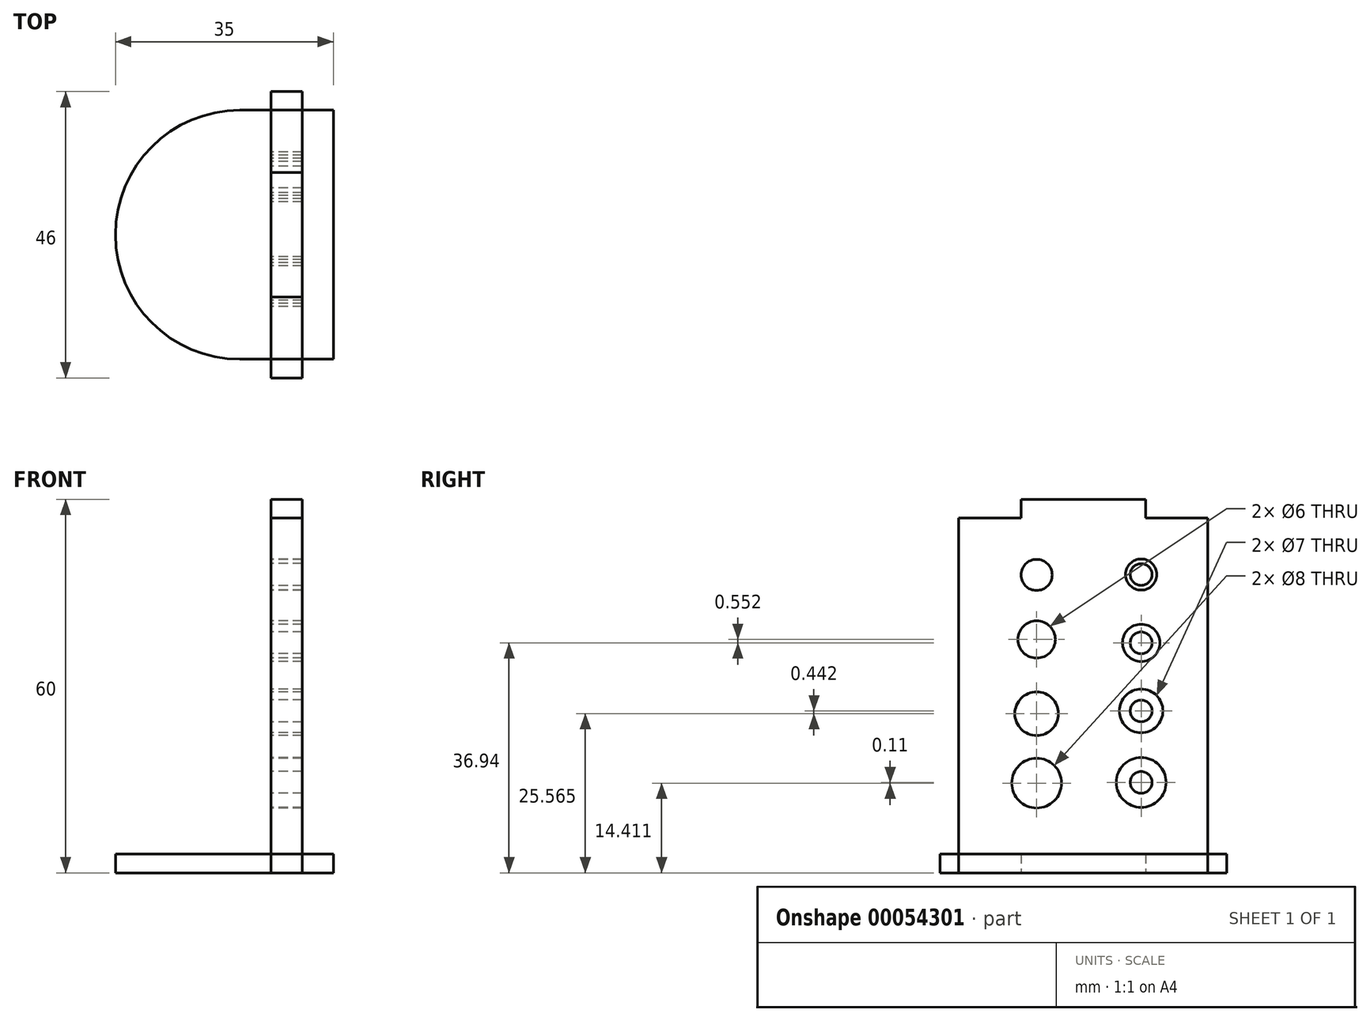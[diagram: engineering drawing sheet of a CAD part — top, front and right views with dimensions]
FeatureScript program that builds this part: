
annotation { "Feature Type Name" : "Feature", "Feature Type Description" : "" }
export const myFeature = defineFeature(function(context is Context, id is Id, definition is map)
    precondition{}
    {
        {
            var Q0;
            Q0=qCreatedBy(makeId("Top.planeOp"),FACE);
            var sketch = newSketch(context, id + "F0", { "sketchPlane" : qUnion([Q0])});
            skLineSegment(sketch, "E0.rect.bottom", {"start": v(7.5, 20) * mm, "end": v(-7.5, 20) * mm});
            skLineSegment(sketch, "E0.rect.top", {"start": v(7.5, -20) * mm, "end": v(-7.5, -20) * mm});
            skLineSegment(sketch, "E0.rect.left", {"start": v(7.5, 20) * mm, "end": v(7.5, -20) * mm});
            skLineSegment(sketch, "E0.rect.right", {"start": v(-7.5, 20) * mm, "end": v(-7.5, -20) * mm});
            skPoint(sketch, "E0.rect.middle", {"position": v(0, 0) * mm});
            skArc(sketch, "E1", {"start": v(-7.5, 20) * mm, "mid": v(-27.5, 0) * mm, "end": v(-7.5, -20) * mm});
            skLineSegment(sketch, "E2.bottom", {"start": v(-2.5, 20) * mm, "end": v(2.5, 20) * mm});
            skLineSegment(sketch, "E2.top", {"start": v(-2.5, 23) * mm, "end": v(2.5, 23) * mm});
            skLineSegment(sketch, "E2.left", {"start": v(-2.5, 20) * mm, "end": v(-2.5, 23) * mm});
            skLineSegment(sketch, "E2.right", {"start": v(2.5, 20) * mm, "end": v(2.5, 23) * mm});
            skLineSegment(sketch, "E3.bottom", {"start": v(-2.5, -20) * mm, "end": v(2.5, -20) * mm});
            skLineSegment(sketch, "E3.top", {"start": v(-2.5, -23) * mm, "end": v(2.5, -23) * mm});
            skLineSegment(sketch, "E3.left", {"start": v(-2.5, -20) * mm, "end": v(-2.5, -23) * mm});
            skLineSegment(sketch, "E3.right", {"start": v(2.5, -20) * mm, "end": v(2.5, -23) * mm});
            skLineSegment(sketch, "E4.bottom", {"start": v(2.5, 20) * mm, "end": v(7.5, 20) * mm});
            skLineSegment(sketch, "E4.top", {"start": v(2.5, 23) * mm, "end": v(7.5, 23) * mm});
            skLineSegment(sketch, "E4.right", {"start": v(7.5, 20) * mm, "end": v(7.5, 23) * mm});
            skLineSegment(sketch, "E5.bottom", {"start": v(2.5, -20) * mm, "end": v(7.5, -20) * mm});
            skLineSegment(sketch, "E5.top", {"start": v(2.5, -23) * mm, "end": v(7.5, -23) * mm});
            skLineSegment(sketch, "E5.right", {"start": v(7.5, -20) * mm, "end": v(7.5, -23) * mm});
            skLineSegment(sketch, "E6.bottom", {"start": v(-2.5, -23) * mm, "end": v(-7.5, -23) * mm});
            skLineSegment(sketch, "E6.top", {"start": v(-2.5, -20) * mm, "end": v(-7.5, -20) * mm});
            skLineSegment(sketch, "E6.left", {"start": v(-2.5, -23) * mm, "end": v(-2.5, -20) * mm});
            skLineSegment(sketch, "E6.right", {"start": v(-7.5, -23) * mm, "end": v(-7.5, -20) * mm});
            skLineSegment(sketch, "E7.bottom", {"start": v(-2.5, 23) * mm, "end": v(-7.5, 23) * mm});
            skLineSegment(sketch, "E7.top", {"start": v(-2.5, 20) * mm, "end": v(-7.5, 20) * mm});
            skLineSegment(sketch, "E7.left", {"start": v(-2.5, 23) * mm, "end": v(-2.5, 20) * mm});
            skLineSegment(sketch, "E7.right", {"start": v(-7.5, 23) * mm, "end": v(-7.5, 20) * mm});
            skArc(sketch, "E8", {"start": v(-7.5, 23) * mm, "mid": v(-30.5, 0) * mm, "end": v(-7.5, -23) * mm});
            skLineSegment(sketch, "E9", {"start": v(7.5, 21.5) * mm, "end": v(-7.5, 21.5) * mm, "construction": true});
            skLineSegment(sketch, "E10", {"start": v(7.5, -21.5) * mm, "end": v(-7.5, -21.5) * mm, "construction": true});
            skArc(sketch, "E11", {"start": v(-7.5, 21.5) * mm, "mid": v(-29, 0) * mm, "end": v(-7.5, -21.5) * mm, "construction": true});
            skLineSegment(sketch, "E12.rect.bottom", {"start": v(2.5, 10) * mm, "end": v(-2.5, 10) * mm});
            skLineSegment(sketch, "E12.rect.top", {"start": v(2.5, -10) * mm, "end": v(-2.5, -10) * mm});
            skLineSegment(sketch, "E12.rect.left", {"start": v(2.5, 10) * mm, "end": v(2.5, -10) * mm});
            skLineSegment(sketch, "E12.rect.right", {"start": v(-2.5, 10) * mm, "end": v(-2.5, -10) * mm});
            skLineSegment(sketch, "E13.rect.bottom", {"start": v(2.5, 20) * mm, "end": v(-2.5, 20) * mm});
            skLineSegment(sketch, "E13.rect.top", {"start": v(2.5, -20) * mm, "end": v(-2.5, -20) * mm});
            skLineSegment(sketch, "E13.rect.left", {"start": v(2.5, 20) * mm, "end": v(2.5, -20) * mm});
            skLineSegment(sketch, "E13.rect.right", {"start": v(-2.5, 20) * mm, "end": v(-2.5, -20) * mm});
            skSolve(sketch);
        }
        {
            var Q0;
            Q0=makeQuery(id+"F0.imprint","IMPRINT",FACE,{"disambiguationData":[TD([[makeQuery(id+"F0.imprint","IMPRINT",EDGE,{"derivedFrom":sQuery(id+"F0.wireOp",EDGE,"E0.rect.right")}),-1.0]])]});
            var Q1;
            Q1=makeQuery(id+"F0.imprint","IMPRINT",FACE,{"disambiguationData":[TD([[makeQuery(id+"F0.imprint","IMPRINT",EDGE,{"derivedFrom":sQuery(id+"F0.wireOp",EDGE,"E0.rect.left")}),-1.0]])]});
            var Q2;
            Q2=makeQuery(id+"F0.imprint","IMPRINT",FACE,{"disambiguationData":[TD([[makeQuery(id+"F0.imprint","IMPRINT",EDGE,{"derivedFrom":sQuery(id+"F0.wireOp",EDGE,"E2.bottom")}),1.0]])]});
            var Q3;
            Q3=makeQuery(id+"F0.imprint","IMPRINT",FACE,{"disambiguationData":[TD([[makeQuery(id+"F0.imprint","IMPRINT",EDGE,{"derivedFrom":sQuery(id+"F0.wireOp",EDGE,"E3.bottom")}),-1.0]])]});
            var Q4;
            Q4=makeQuery(id+"F0.imprint","IMPRINT",FACE,{"disambiguationData":[TD([[makeQuery(id+"F0.imprint","IMPRINT",EDGE,{"derivedFrom":sQuery(id+"F0.wireOp",EDGE,"E0.rect.right")}),1.0]])]});
            var Q5;
            {var subQ0=sQuery(id+"F0.wireOp",EDGE,"E12.rect.bottom");Q5=makeQuery(id+"F0.imprint","IMPRINT",FACE,{"disambiguationData":[TD([[makeQuery(id+"F0.imprint","IMPRINT",EDGE,{"derivedFrom":subQ0}),-1.0]])]});}
            var Q6;
            {var subQ0=sQuery(id+"F0.wireOp",EDGE,"E12.rect.top");Q6=makeQuery(id+"F0.imprint","IMPRINT",FACE,{"disambiguationData":[TD([[makeQuery(id+"F0.imprint","IMPRINT",EDGE,{"derivedFrom":subQ0}),1.0]])]});}
            var Q7;
            Q7=makeQuery(id+"F0.imprint","IMPRINT",FACE,{"disambiguationData":[TD([[makeQuery(id+"F0.imprint","IMPRINT",EDGE,{"derivedFrom":sQuery(id+"F0.wireOp",EDGE,"E2.top")}),-1.0]])]});
            var Q8;
            Q8=makeQuery(id+"F0.imprint","IMPRINT",FACE,{"disambiguationData":[TD([[makeQuery(id+"F0.imprint","IMPRINT",EDGE,{"derivedFrom":sQuery(id+"F0.wireOp",EDGE,"E3.top")}),1.0]])]});
            extrude(context, id + "F1", {"entities" : qUnion([Q0, Q1, Q2, Q3, Q4, Q5, Q6, Q7, Q8]), "depth" : 3 * mm});
        }
        {
            var Q0;
            {var subQ0=sQuery(id+"F0.wireOp",EDGE,"E12.rect.bottom");Q0=makeQuery(id+"F0.imprint","IMPRINT",FACE,{"disambiguationData":[TD([[makeQuery(id+"F0.imprint","IMPRINT",EDGE,{"derivedFrom":subQ0}),1.0]])]});}
            var Q1;
            {var subQ0=sQuery(id+"F0.wireOp",EDGE,"E12.rect.bottom");Q1=makeQuery(id+"F0.imprint","IMPRINT",FACE,{"disambiguationData":[TD([[makeQuery(id+"F0.imprint","IMPRINT",EDGE,{"derivedFrom":subQ0}),-1.0]])]});}
            var Q2;
            {var subQ0=sQuery(id+"F0.wireOp",EDGE,"E12.rect.top");Q2=makeQuery(id+"F0.imprint","IMPRINT",FACE,{"disambiguationData":[TD([[makeQuery(id+"F0.imprint","IMPRINT",EDGE,{"derivedFrom":subQ0}),1.0]])]});}
            extrude(context, id + "F2", {"entities" : qUnion([Q0, Q1, Q2]), "depth" : 60 * mm});
        }
        {
            var Q0;
            {var subQ0=sQuery(id+"F0.wireOp",EDGE,"E12.rect.bottom");Q0=makeQuery(id+"F0.imprint","IMPRINT",FACE,{"disambiguationData":[TD([[makeQuery(id+"F0.imprint","IMPRINT",EDGE,{"derivedFrom":subQ0}),-1.0]])]});}
            var Q1;
            {var subQ0=sQuery(id+"F0.wireOp",EDGE,"E12.rect.top");Q1=makeQuery(id+"F0.imprint","IMPRINT",FACE,{"disambiguationData":[TD([[makeQuery(id+"F0.imprint","IMPRINT",EDGE,{"derivedFrom":subQ0}),1.0]])]});}
            extrude(context, id + "F3", {"entities" : qUnion([Q0, Q1]), "operationType" : NewBodyOperationType.REMOVE, "depth" : 3 * mm});
        }
        {
            var Q0;
            Q0=makeQuery(id+"F2.opExtrude","CAP_FACE",FACE,{"disambiguationData":[OSD([sQuery(id+"F0.wireOp",EDGE,"E13.rect.bottom"),sQuery(id+"F0.wireOp",EDGE,"E13.rect.top"),sQuery(id+"F0.wireOp",EDGE,"E13.rect.left"),sQuery(id+"F0.wireOp",EDGE,"E13.rect.right")])],"isStart":false});
            var sketch = newSketch(context, id + "F4", { "sketchPlane" : qUnion([Q0])});
            skLineSegment(sketch, "E14.0.0", {"start": v(2.5, -10) * mm, "end": v(2.5, 10) * mm});
            skLineSegment(sketch, "E14.0.1", {"start": v(2.5, 10) * mm, "end": v(-2.5, 10) * mm});
            skLineSegment(sketch, "E14.0.2", {"start": v(-2.5, 10) * mm, "end": v(-2.5, -10) * mm});
            skLineSegment(sketch, "E14.0.3", {"start": v(-2.5, -10) * mm, "end": v(2.5, -10) * mm});
            skLineSegment(sketch, "E15.top", {"start": v(-2.5, -20) * mm, "end": v(2.5, -20) * mm});
            skLineSegment(sketch, "E15.left", {"start": v(-2.5, -10) * mm, "end": v(-2.5, -20) * mm});
            skLineSegment(sketch, "E15.right", {"start": v(2.5, -10) * mm, "end": v(2.5, -20) * mm});
            skLineSegment(sketch, "E16.bottom", {"start": v(2.5, 20) * mm, "end": v(-2.5, 20) * mm});
            skLineSegment(sketch, "E16.left", {"start": v(2.5, 20) * mm, "end": v(2.5, 10) * mm});
            skLineSegment(sketch, "E16.right", {"start": v(-2.5, 20) * mm, "end": v(-2.5, 10) * mm});
            skSolve(sketch);
        }
        {
            var Q0;
            Q0=makeQuery(id+"F4.imprint","IMPRINT",FACE,{"disambiguationData":[TD([[makeQuery(id+"F4.imprint","IMPRINT",EDGE,{"derivedFrom":sQuery(id+"F4.wireOp",EDGE,"E14.0.3")}),-1.0]])]});
            var Q1;
            Q1=makeQuery(id+"F4.imprint","IMPRINT",FACE,{"disambiguationData":[TD([[makeQuery(id+"F4.imprint","IMPRINT",EDGE,{"derivedFrom":sQuery(id+"F4.wireOp",EDGE,"E16.bottom")}),1.0]])]});
            extrude(context, id + "F5", {"entities" : qUnion([Q0, Q1]), "operationType" : NewBodyOperationType.REMOVE, "oppositeDirection" : true, "depth" : 3 * mm});
        }
        {
            var Q0;
            Q0=makeQuery(id+"F2.opExtrude","SWEPT_FACE",FACE,{"disambiguationData":[OSD([sQuery(id+"F0.wireOp",EDGE,"E13.rect.right")])]});
            var sketch = newSketch(context, id + "F6", { "sketchPlane" : qUnion([Q0])});
            skCircle(sketch, "E17", {"center": v(-9.29, 47.92) * mm, "radius": 1.75 * mm});
            skCircle(sketch, "E18", {"center": v(-9.29, 47.92) * mm, "radius": 2.5 * mm});
            skCircle(sketch, "E19", {"center": v(7.5, 47.86) * mm, "radius": 2.5 * mm});
            skCircle(sketch, "E20", {"center": v(-9.29, 36.94) * mm, "radius": 3 * mm});
            skCircle(sketch, "E21", {"center": v(-9.29, 26) * mm, "radius": 3.5 * mm});
            skCircle(sketch, "E22", {"center": v(-9.29, 14.52) * mm, "radius": 4 * mm});
            skCircle(sketch, "E23", {"center": v(7.5, 37.5) * mm, "radius": 3 * mm});
            skCircle(sketch, "E24", {"center": v(7.5, 25.57) * mm, "radius": 3.5 * mm});
            skCircle(sketch, "E25", {"center": v(7.5, 14.41) * mm, "radius": 4 * mm});
            skCircle(sketch, "E26", {"center": v(-9.29, 36.94) * mm, "radius": 1.75 * mm});
            skCircle(sketch, "E27", {"center": v(-9.29, 26) * mm, "radius": 1.75 * mm});
            skCircle(sketch, "E28", {"center": v(-9.29, 14.52) * mm, "radius": 1.75 * mm});
            skLineSegment(sketch, "E29.0", {"start": v(-10, 60) * mm, "end": v(10, 60) * mm});
            skLineSegment(sketch, "E30.0", {"start": v(10, 57) * mm, "end": v(10, 60) * mm});
            skLineSegment(sketch, "E31.0", {"start": v(10, 57) * mm, "end": v(20, 57) * mm});
            skLineSegment(sketch, "E32.0", {"start": v(20, 57) * mm, "end": v(20, 3) * mm});
            skLineSegment(sketch, "E33", {"start": v(20, 3) * mm, "end": v(10, 3) * mm});
            skLineSegment(sketch, "E34", {"start": v(10, 3) * mm, "end": v(10, 0) * mm});
            skLineSegment(sketch, "E35", {"start": v(10, 0) * mm, "end": v(-10, 0) * mm});
            skLineSegment(sketch, "E36", {"start": v(-10, 0) * mm, "end": v(-10, 3) * mm});
            skLineSegment(sketch, "E37", {"start": v(-10, 3) * mm, "end": v(-20, 3) * mm});
            skLineSegment(sketch, "E38", {"start": v(-20, 3) * mm, "end": v(-20, 57) * mm});
            skLineSegment(sketch, "E39", {"start": v(-20, 57) * mm, "end": v(-10, 57) * mm});
            skLineSegment(sketch, "E40", {"start": v(-10, 57) * mm, "end": v(-10, 60) * mm});
            skSolve(sketch);
        }
        {
            var Q0;
            Q0=makeQuery(id+"F6.imprint","IMPRINT",FACE,{"disambiguationData":[TD([[makeQuery(id+"F6.imprint","IMPRINT",EDGE,{"derivedFrom":sQuery(id+"F6.wireOp",EDGE,"E19")}),1.0]])]});
            var Q1;
            Q1=makeQuery(id+"F6.imprint","IMPRINT",FACE,{"disambiguationData":[TD([[makeQuery(id+"F6.imprint","IMPRINT",EDGE,{"derivedFrom":sQuery(id+"F6.wireOp",EDGE,"E23")}),1.0]])]});
            var Q2;
            Q2=makeQuery(id+"F6.imprint","IMPRINT",FACE,{"disambiguationData":[TD([[makeQuery(id+"F6.imprint","IMPRINT",EDGE,{"derivedFrom":sQuery(id+"F6.wireOp",EDGE,"E24")}),1.0]])]});
            var Q3;
            Q3=makeQuery(id+"F6.imprint","IMPRINT",FACE,{"disambiguationData":[TD([[makeQuery(id+"F6.imprint","IMPRINT",EDGE,{"derivedFrom":sQuery(id+"F6.wireOp",EDGE,"E25")}),1.0]])]});
            var Q4;
            Q4=makeQuery(id+"F6.imprint","IMPRINT",FACE,{"disambiguationData":[TD([[makeQuery(id+"F6.imprint","IMPRINT",EDGE,{"derivedFrom":sQuery(id+"F6.wireOp",EDGE,"E22")}),1.0]])]});
            var Q5;
            Q5=makeQuery(id+"F6.imprint","IMPRINT",FACE,{"disambiguationData":[TD([[makeQuery(id+"F6.imprint","IMPRINT",EDGE,{"derivedFrom":sQuery(id+"F6.wireOp",EDGE,"E21")}),1.0]])]});
            var Q6;
            Q6=makeQuery(id+"F6.imprint","IMPRINT",FACE,{"disambiguationData":[TD([[makeQuery(id+"F6.imprint","IMPRINT",EDGE,{"derivedFrom":sQuery(id+"F6.wireOp",EDGE,"E20")}),1.0]])]});
            var Q7;
            Q7=makeQuery(id+"F6.imprint","IMPRINT",FACE,{"disambiguationData":[TD([[makeQuery(id+"F6.imprint","IMPRINT",EDGE,{"derivedFrom":sQuery(id+"F6.wireOp",EDGE,"E17")}),-1.0]])]});
            extrude(context, id + "F7", {"entities" : qUnion([Q0, Q1, Q2, Q3, Q4, Q5, Q6, Q7]), "operationType" : NewBodyOperationType.REMOVE, "endBound" : BoundingType.UP_TO_NEXT, "oppositeDirection" : true, "depth" : 25 * mm});
        }
    });
